# Revit family: Gira_547300
name_source: partatom
category: Elektroinstallationen
revit_build: Autodesk Revit 2017 (Build: 20160225_1515(x64)
units: mm (PartAtom-declared; Revit-internal decimal feet)

## family parameters
Basisbauteil = Fläche
Beim Laden mit Abzugskörper schneiden = Nein
Bemaßung runder Anschluss = Durchmesser verwenden
Beschriftungsausrichtung beibehalten = Nein
Gemeinsam genutzt = Nein
Raumberechnungspunkt = Nein
Teiletyp = Normal

## types (1)
- Funk Energiesensor 4f REG Gira eNet
    Andere Bussysteme = eNet
    Anschlussart = direkt
    Anzahl der Ausgänge = 0
    Anzahl der binären Eingänge = 0
    Ausführung Text = Energie-Zähler
    BIM = https://media.stage.bim.site 8f.rfa
    BIMSITE_PRODUCT_ID = 996cdf7b99e2f293fb83e3a053500779b17a33f8
    Beschreibung = eNet Funk Energiesensor 4fach  REG Merkmale:  Die eNet Funk Energiesensoren ermöglichen die Funkübertragung von Spannungs-, Strom- und Energiewerten an den eNet Server.  Betrieb mit eNet Server.  Erfassen von Strom und Spannung des angeschlossenen Verbrauchers.  Berechnen der Wirkleistung, der Blindleistung, der Scheinleistung und der elektrischen Wirkenergie.  Ereignis- oder zeitgesteuertes Senden von Messwerttelegrammen an den eNet Server.  Synchronisation der Uhrzeit mit dem eNet Server.  Anzeige eines einzelnen Energiewertes ist über die eNet SMART HOME app möglich.  Nutzung der Energiewerte als Auslöser für Wenn-Dann-Regeln in der eNet SMART HOME app. Mit eNet Server einstellbar::  Lokalisierung des Geräts.  Vollverschlüsselte Funkübertragung (AES-CCM) ab eNet Server Software Version 2.0.  Energieverbräuche als Wenn-Bedingung in Wenn-Dann-Regeln nutzen, um Aktionen, Szenen und Zeitschaltuhren zu aktivieren.  Update der Gerätesoftware.  Hinweise :  Zum Betrieb dieses Reiheneinbaugeräts wird ein eNet Server benötigt.
    Blindleistung = Nein
    Breite in Teilungseinheiten = 0
    Bussystem Funkbus = Ja
    Bussystem KNX = Nein
    Bussystem KNX-Funk = Nein
    Bussystem LON = Nein
    Bussystem Powernet = Ja
    Datenblatt = https://media.stage.bim.site
    Datenblatt 1 = https://media.stage.bim.site
    GTIN = 4010337774372
    Geeignet für C-Last = Nein
    HAN = 547300
    HeinzeBIM = https://www.heinze.de
    Hersteller = Gira
    Kosten = 0 $
    Max. Anzahl der Schaltausgänge = 0
    Mit Busankopplung = Nein
    Mit LED-Anzeige = Nein
    Produktseite = https://media.stage.bim.site
    S0 Impulsschnittstelle = ohne
    Tarifumschaltung = Nein
    Typname = Funk Energiesensor 4f REG Gira eNet
    URL = https://www.gira.de
    Vor Ort-/Handbedienung = Nein
    Vorgabe-Ansicht = 1219 mm
    Zulassung nach PTB = Nein

## geometry (parser evidence)
native form markers: Sweep x3
no freeform markers — native parametric forms only
